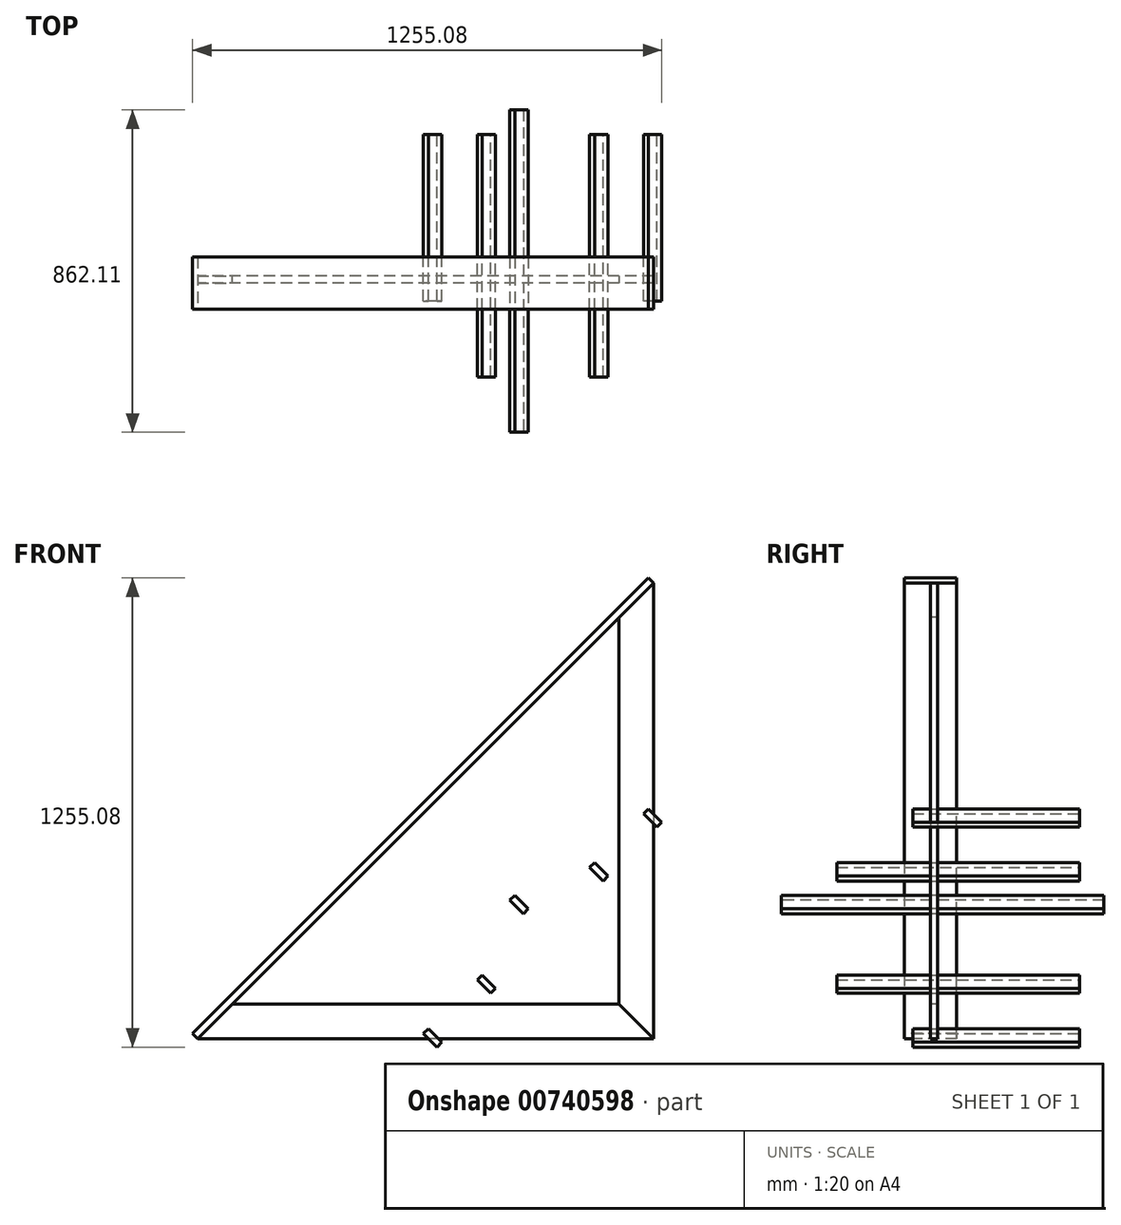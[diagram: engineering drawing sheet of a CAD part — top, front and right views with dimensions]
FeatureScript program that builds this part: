
annotation { "Feature Type Name" : "Feature", "Feature Type Description" : "" }
export const myFeature = defineFeature(function(context is Context, id is Id, definition is map)
    precondition{}
    {
        {
            var Q0;
            Q0=qCreatedBy(makeId("Front.planeOp"),FACE);
            var sketch = newSketch(context, id + "F0", { "sketchPlane" : qUnion([Q0])});
            skLineSegment(sketch, "E0.bottom", {"start": v(609.6, -46.04) * mm, "end": v(-609.6, -46.04) * mm});
            skLineSegment(sketch, "E1", {"start": v(609.6, -46.04) * mm, "end": v(517.52, 46.04) * mm});
            skLineSegment(sketch, "E2", {"start": v(517.52, 46.04) * mm, "end": v(-517.53, 46.04) * mm});
            skLineSegment(sketch, "E3", {"start": v(-609.6, -46.04) * mm, "end": v(-517.52, 46.04) * mm});
            skSolve(sketch);
        }
        {
            var Q0;
            Q0=makeQuery(id+"F0.imprint","IMPRINT",FACE,{"disambiguationData":[TD([[makeQuery(id+"F0.imprint","IMPRINT",EDGE,{"derivedFrom":sQuery(id+"F0.wireOp",EDGE,"E0.bottom")}),-1.0]])]});
            extrude(context, id + "F1", {"entities" : qUnion([Q0]), "oppositeDirection" : true, "depth" : 19.05 * mm, "offsetDistance" : 25.4 * mm});
        }
        {
            var Q0;
            Q0=qCreatedBy(makeId("Front.planeOp"),FACE);
            var sketch = newSketch(context, id + "F2", { "sketchPlane" : qUnion([Q0])});
            skLineSegment(sketch, "E4", {"start": v(609.6, -46.04) * mm, "end": v(517.52, 46.04) * mm});
            skLineSegment(sketch, "E5", {"start": v(517.52, 46.04) * mm, "end": v(517.52, 1081.09) * mm});
            skLineSegment(sketch, "E6", {"start": v(609.6, 1173.16) * mm, "end": v(609.6, -46.04) * mm});
            skLineSegment(sketch, "E7", {"start": v(609.6, 1173.16) * mm, "end": v(517.52, 1081.09) * mm});
            skSolve(sketch);
        }
        {
            var Q0;
            Q0=makeQuery(id+"F2.imprint","IMPRINT",FACE,{"disambiguationData":[TD([[makeQuery(id+"F2.imprint","IMPRINT",EDGE,{"derivedFrom":sQuery(id+"F2.wireOp",EDGE,"E4")}),-1.0]])]});
            extrude(context, id + "F3", {"entities" : qUnion([Q0]), "oppositeDirection" : true, "depth" : 19.05 * mm, "offsetDistance" : 25.4 * mm});
        }
        {
            var Q0;
            Q0=makeQuery(id+"F1.opExtrude","CAP_VERTEX",VERTEX,{"disambiguationData":[OSD([sQuery(id+"F0.wireOp",EDGE,"E0.bottom"),sQuery(id+"F0.wireOp",EDGE,"E3")])],"isStart":false});
            var Q1;
            Q1=makeQuery(id+"F1.opExtrude","CAP_VERTEX",VERTEX,{"disambiguationData":[OSD([sQuery(id+"F0.wireOp",EDGE,"E0.bottom"),sQuery(id+"F0.wireOp",EDGE,"E3")])],"isStart":true});
            var Q2;
            Q2=makeQuery(id+"F3.opExtrude","CAP_VERTEX",VERTEX,{"disambiguationData":[OSD([sQuery(id+"F2.wireOp",EDGE,"E6"),sQuery(id+"F2.wireOp",EDGE,"E7")])],"isStart":true});
            cPlane(context, id + "F4", {"entities" : qUnion([Q0, Q1, Q2]), "cplaneType" : CPlaneType.THREE_POINT, "offset" : 5.08 * mm, "width" : 152.4 * mm, "height" : 152.4 * mm});
        }
        {
            var Q0;
            Q0=qCreatedBy(id+"F4.planeOp",FACE);
            var sketch = newSketch(context, id + "F5", { "sketchPlane" : qUnion([Q0])});
            skLineSegment(sketch, "E8", {"start": v(69.85, -463.6) * mm, "end": v(-69.85, -463.6) * mm});
            skLineSegment(sketch, "E9", {"start": v(69.85, -463.6) * mm, "end": v(69.85, 1260.6) * mm});
            skLineSegment(sketch, "E10", {"start": v(69.85, 1260.6) * mm, "end": v(-69.85, 1260.6) * mm});
            skLineSegment(sketch, "E11", {"start": v(-69.85, 1260.6) * mm, "end": v(-69.85, -463.6) * mm});
            skSolve(sketch);
        }
        {
            var Q0;
            Q0=makeQuery(id+"F5.imprint","IMPRINT",FACE,{"disambiguationData":[TD([[makeQuery(id+"F5.imprint","IMPRINT",EDGE,{"derivedFrom":sQuery(id+"F5.wireOp",EDGE,"E8")}),-1.0]])]});
            extrude(context, id + "F6", {"entities" : qUnion([Q0]), "oppositeDirection" : true, "depth" : 19.05 * mm, "offsetDistance" : 25.4 * mm});
        }
        {
            var Q0;
            Q0=makeQuery(id+"F1.opExtrude","SWEPT_FACE",FACE,{"disambiguationData":[OSD([sQuery(id+"F0.wireOp",EDGE,"E1")])]});
            cPlane(context, id + "F7", {"entities" : qUnion([Q0]), "cplaneType" : CPlaneType.OFFSET, "offset" : 0 * mm, "width" : 152.4 * mm, "height" : 152.4 * mm});
        }
        {
            var Q0;
            Q0=qCreatedBy(id+"F7.planeOp",FACE);
            var sketch = newSketch(context, id + "F8", { "sketchPlane" : qUnion([Q0])});
            skLineSegment(sketch, "E12.bottom", {"start": v(463.6, 69.85) * mm, "end": v(-398.5, 69.85) * mm});
            skLineSegment(sketch, "E12.top", {"start": v(463.6, 19.05) * mm, "end": v(-398.5, 19.05) * mm});
            skLineSegment(sketch, "E12.left", {"start": v(463.6, 69.85) * mm, "end": v(463.6, 19.05) * mm});
            skLineSegment(sketch, "E12.right", {"start": v(-398.5, 69.85) * mm, "end": v(-398.5, 19.05) * mm});
            skSolve(sketch);
        }
        {
            var Q0;
            Q0=makeQuery(id+"F8.imprint","IMPRINT",FACE,{"disambiguationData":[TD([[makeQuery(id+"F8.imprint","IMPRINT",EDGE,{"derivedFrom":sQuery(id+"F8.wireOp",EDGE,"E12.bottom")}),1.0]])]});
            extrude(context, id + "F9", {"entities" : qUnion([Q0]), "endBound" : BoundingType.SYMMETRIC, "depth" : 19.05 * mm, "offsetDistance" : 25.4 * mm});
        }
        {
            var Q0;
            Q0=makeQuery(id+"F9.opExtrude","CAP_FACE",FACE,{"disambiguationData":[OSD([sQuery(id+"F8.wireOp",EDGE,"E12.bottom"),sQuery(id+"F8.wireOp",EDGE,"E12.top"),sQuery(id+"F8.wireOp",EDGE,"E12.left"),sQuery(id+"F8.wireOp",EDGE,"E12.right")])],"isStart":true});
            cPlane(context, id + "F10", {"entities" : qUnion([Q0]), "cplaneType" : CPlaneType.OFFSET, "offset" : 203.2 * mm, "width" : 152.4 * mm, "height" : 152.4 * mm});
        }
        {
            var Q0;
            Q0=qCreatedBy(id+"F10.planeOp",FACE);
            var sketch = newSketch(context, id + "F11", { "sketchPlane" : qUnion([Q0])});
            skLineSegment(sketch, "E13.bottom", {"start": v(250.88, -69.85) * mm, "end": v(-398.5, -69.85) * mm});
            skLineSegment(sketch, "E13.top", {"start": v(250.88, -19.05) * mm, "end": v(-398.5, -19.05) * mm});
            skLineSegment(sketch, "E13.left", {"start": v(250.88, -69.85) * mm, "end": v(250.88, -19.05) * mm});
            skLineSegment(sketch, "E13.right", {"start": v(-398.5, -69.85) * mm, "end": v(-398.5, -19.05) * mm});
            skSolve(sketch);
        }
        {
            var Q0;
            Q0 = qSketchRegion(id + "F11", true);
            extrude(context, id + "F12", {"entities" : qUnion([Q0]), "endBound" : BoundingType.SYMMETRIC, "depth" : 19.05 * mm, "offsetDistance" : 25.4 * mm});
        }
        {
            var Q0;
            Q0=qCreatedBy(id+"F10.planeOp",FACE);
            cPlane(context, id + "F13", {"entities" : qUnion([Q0]), "cplaneType" : CPlaneType.OFFSET, "offset" : 203.2 * mm, "width" : 152.4 * mm, "height" : 152.4 * mm});
        }
        {
            var Q0;
            Q0=qCreatedBy(id+"F13.planeOp",FACE);
            var sketch = newSketch(context, id + "F14", { "sketchPlane" : qUnion([Q0])});
            skLineSegment(sketch, "E14.bottom", {"start": v(47.68, -69.85) * mm, "end": v(-398.5, -69.85) * mm});
            skLineSegment(sketch, "E15", {"start": v(47.68, -69.85) * mm, "end": v(47.68, -19.05) * mm});
            skLineSegment(sketch, "E16", {"start": v(47.68, -19.05) * mm, "end": v(-398.5, -19.05) * mm});
            skLineSegment(sketch, "E17", {"start": v(-398.5, -19.05) * mm, "end": v(-398.5, -69.85) * mm});
            skSolve(sketch);
        }
        {
            var Q0;
            Q0 = qSketchRegion(id + "F14", true);
            extrude(context, id + "F15", {"entities" : qUnion([Q0]), "endBound" : BoundingType.SYMMETRIC, "depth" : 19.05 * mm, "offsetDistance" : 25.4 * mm});
        }
        {
            var Q0;
            Q0=makeQuery(id+"F15.opExtrude","SWEPT_BODY",BODY,{"disambiguationData":[OSD([sQuery(id+"F14.wireOp",EDGE,"E14.bottom"),sQuery(id+"F14.wireOp",EDGE,"E15"),sQuery(id+"F14.wireOp",EDGE,"E16"),sQuery(id+"F14.wireOp",EDGE,"E17")])]});
            var Q1;
            Q1=makeQuery(id+"F12.opExtrude","SWEPT_BODY",BODY,{"disambiguationData":[OSD([sQuery(id+"F11.wireOp",EDGE,"E13.bottom"),sQuery(id+"F11.wireOp",EDGE,"E13.top"),sQuery(id+"F11.wireOp",EDGE,"E13.left"),sQuery(id+"F11.wireOp",EDGE,"E13.right")])]});
            var Q2;
            Q2=qCreatedBy(id+"F7.planeOp",FACE);
            mirror(context, id + "F16", {"entities" : qUnion([Q0, Q1]), "mirrorPlane" : qUnion([Q2])});
        }
    });
